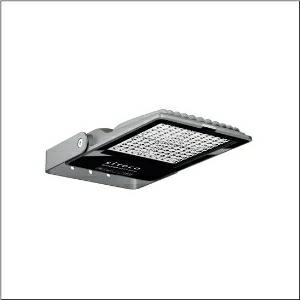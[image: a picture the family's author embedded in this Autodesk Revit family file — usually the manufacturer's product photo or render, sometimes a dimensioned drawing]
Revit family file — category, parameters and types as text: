
# Revit family: sicompact_r__31_mini___pl32_5xa7571f1k23_4385
name_source: partatom
category: Lighting Fixtures
units: mm (PartAtom-declared; Revit-internal decimal feet)

## family parameters
Cut with Voids When Loaded = No
Host = Face
Light Source = No
Part Type = Normal
Room Calculation Point = No
Round Connector Dimension = Use Diameter
Shared = No

## types (1)
- SiCompact® 31 mini  PL32 (1 x LED, 20000 lm, 130 W, 3000K)
    Apparent Load = 130 VA
    CIE Flux Codes = 32 69 98 100 100
    Color Rendering = 70
    Color Temperature = 3000K
    Default Elevation = 1800 mm
    Description = SiCompact® 31 mini, floodlight, primary light control with lens, of plastic, of toughened safety glass, transparent, light distribution: PL32, light emission: direct distribution, primary light characteristic: asymmetric, installation type: surface-mounted, LED, High Power LED, rated luminous flux: 20.000lm, luminous efficacy: 154lm/W, light colour: 730, colour temperature: 3000K, control gear: ON/OFF, with cable, 3x 1.5mm², mains connection: 220..240V, AC, 50/60Hz, connection cable pre-assembled, cable length: 2m, rated input power: 130W, of diecast aluminium, specular, metallic grey (RAL 9006), length: 461mm, width: 261mm, height: 62mm, bracket, of sheet steel, coated, metallic grey (RAL 9006), ON/OFF, protection rating (complete): IP66, insulation class (complete): insulation class I (protective earthing), certification: CE, ENEC, impact resistance: IK08, permissible operating ambient temperature: -40..+45°C, packaging unit: 1 piece

Light Distribution: PL32
    Height = 62 mm  [stored 0.203412 ft]
    Lamp = 1 x LED
    Lamp Light Flux = 20000 lm
    Lamp Power = 130 W
    Lamp count = 1
    Length = 460 mm
    Luminous efficacy = 154 lm/W
    Manufacturer = Siteco
    ModVariant = No
    Model = 5XA7571F1K23
    Mounting Place = Wall
    Mounting Type = Surface mounted
    Number of Poles = 1
    OnlyDefault = Yes
    Power Factor = 1
    Product Name = SiCompact® 31 mini | PL32
    Product group = floodlight | wall mounted
    ProductGroupID = 2001
    Protection Class = Protection class I
    Protection Degree = IP 66
    RLX_Detail_Level = 1
    RLX_Emergency_Light_Flux = 0 lm
    RLX_Emergency_Type = 0
    RLX_Emergency_Type_DB = No
    RlxData = <blob elided: 126553 chars, md5=e00914a7>
    Socket = socket
    Standby Power = 0 W
    System Light Flux = 20000 lm
    System Power = 130 W
    Type Comments = Product without accessories
    Type Image = l_1006951.jpg
    URL = http://relux.com
    VarID = ---
    Voltage = 0 V
    Weight = 0.00 kg
    Width = 260 mm

note: [stored X ft] marks values corroborated as IEEE doubles in the binary element streams (Revit-internal decimal feet)

## geometry (parser evidence)
native form markers: Blend x4, Sweep x15
no freeform markers — native parametric forms only
